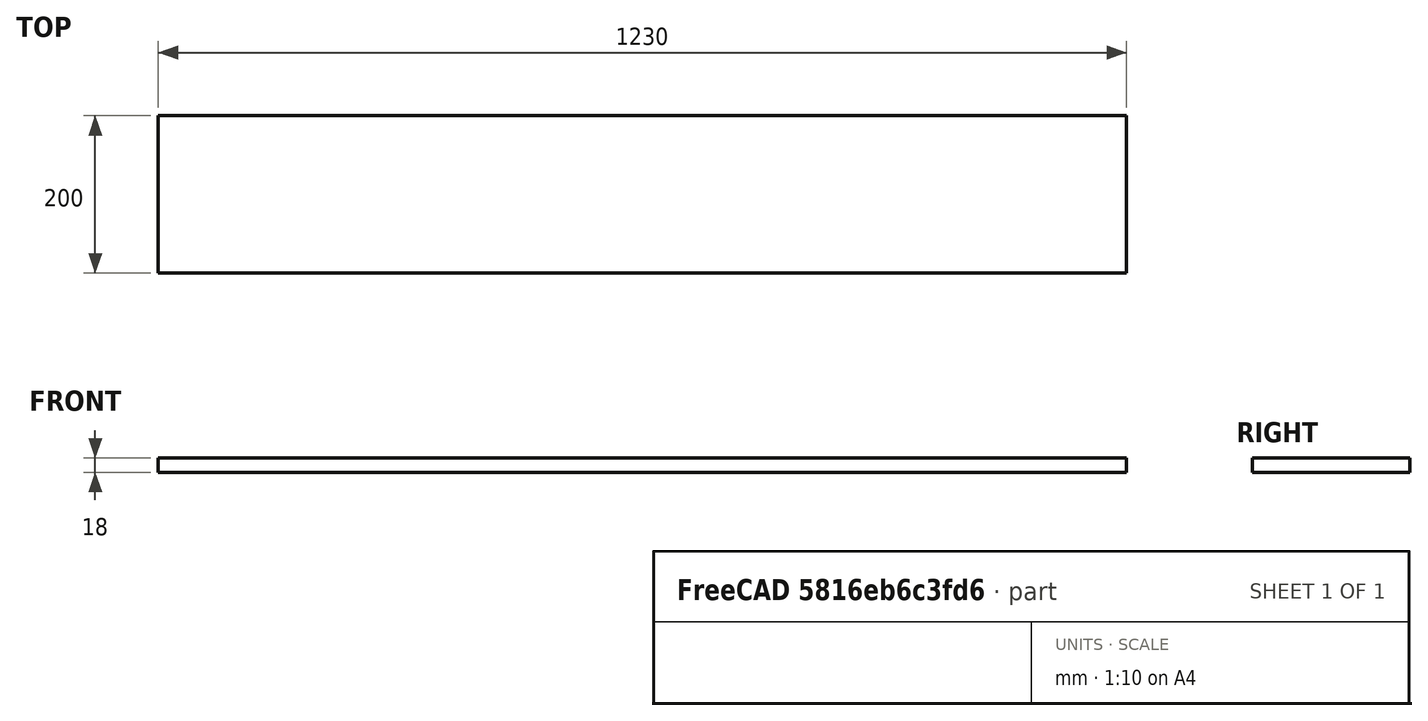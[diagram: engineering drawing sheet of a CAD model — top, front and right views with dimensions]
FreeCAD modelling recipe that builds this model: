
FCSTD DOCUMENT  (FreeCAD 1.0R39109 (Git))
Label: 31_shelf_base_long
License: All rights reserved
LicenseURL: http://en.wikipedia.org/wiki/All_rights_reserved
objects: Spreadsheet::Sheet×1, Sketcher::SketchObject×1, PartDesign::Pad×1, PartDesign::Body×1
note: 6 computed .brp shape members not serialized (recipe doc carries the construction recipe); baked Part::Feature solids carry a one-line shape summary decoded from their .brp

FEATURE [Spreadsheet::Sheet] Spreadsheet
  cells = A2='length; B2(length)=1230; A3='width; B3(width)=200; A4='height; B4(height)=18
FEATURE [Sketcher::SketchObject] Sketch
  ArcFitTolerance = 0
  AttachmentSupport = -> [XY_Plane]
  FullyConstrained = true
  MakeInternals = false
  MapMode = 5
  expr: Constraints[11] = Spreadsheet.length
  expr: Constraints[12] = Spreadsheet.width
  sketch-geometry (5):
    g0: LineSegment StartX=-615 StartY=100 StartZ=0 EndX=615 EndY=100 EndZ=0
    g1: LineSegment StartX=615 StartY=100 StartZ=0 EndX=615 EndY=-100 EndZ=0
    g2: LineSegment StartX=615 StartY=-100 StartZ=0 EndX=-615 EndY=-100 EndZ=0
    g3: LineSegment StartX=-615 StartY=-100 StartZ=0 EndX=-615 EndY=100 EndZ=0
    g4: LineSegment [constr] StartX=-615 StartY=100 StartZ=0 EndX=615 EndY=-100 EndZ=0
  constraints (13):
    c: Coincident(g0,g1)
    c: Coincident(g1,g2)
    c: Coincident(g2,g3)
    c: Coincident(g3,g0)
    c: Horizontal(g0)
    c: Horizontal(g2)
    c: Vertical(g1)
    c: Vertical(g3)
    c: Coincident(g4,g1)
    c: Coincident(g0,g4)
    c: Symmetric(g0,g1,g-1)
    c: Distance(g0,g0) = 1230
    c: Distance(g0,g2) = 200
FEATURE [PartDesign::Pad] Pad
  Direction = (0,0,1)
  Length = 18
  Length2 = 10
  Profile = -> Sketch
  ReferenceAxis = -> Sketch [N_Axis]
  Suppressed = false
  Type = 0
  expr: Length = Spreadsheet.height
FEATURE [PartDesign::Body] Body
  AllowCompound = false
  Group = -> [Sketch,Pad]
  Origin = -> Origin
  Tip = -> Pad
